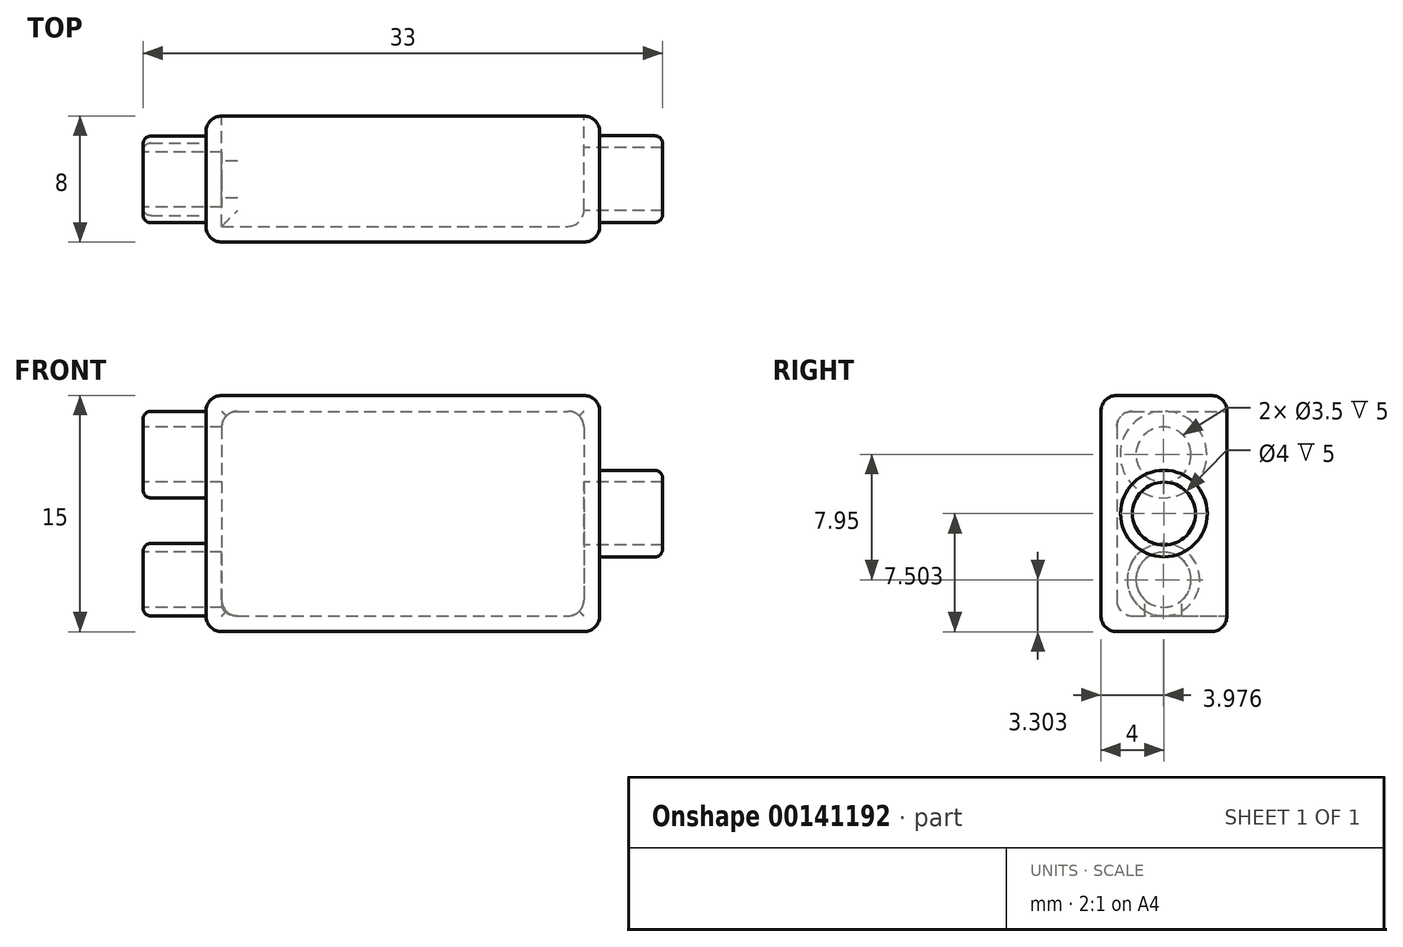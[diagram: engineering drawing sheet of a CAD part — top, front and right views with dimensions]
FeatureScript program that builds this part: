
annotation { "Feature Type Name" : "Feature", "Feature Type Description" : "" }
export const myFeature = defineFeature(function(context is Context, id is Id, definition is map)
    precondition{}
    {
        {
            var Q0;
            Q0=qCreatedBy(makeId("Front.planeOp"),FACE);
            var sketch = newSketch(context, id + "F0", { "sketchPlane" : qUnion([Q0])});
            skLineSegment(sketch, "E0.bottom", {"start": v(-13.07, 10.1) * mm, "end": v(11.93, 10.1) * mm});
            skLineSegment(sketch, "E0.top", {"start": v(-13.07, -4.9) * mm, "end": v(11.93, -4.9) * mm});
            skLineSegment(sketch, "E0.left", {"start": v(-13.07, 10.1) * mm, "end": v(-13.07, -4.9) * mm});
            skLineSegment(sketch, "E0.right", {"start": v(11.93, 10.1) * mm, "end": v(11.93, -4.9) * mm});
            skSolve(sketch);
        }
        {
            var Q0;
            Q0=makeQuery(id+"F0.imprint","IMPRINT",FACE,{"disambiguationData":[TD([[makeQuery(id+"F0.imprint","IMPRINT",EDGE,{"derivedFrom":sQuery(id+"F0.wireOp",EDGE,"E0.bottom")}),-1.0]])]});
            extrude(context, id + "F1", {"entities" : qUnion([Q0]), "depth" : 8 * mm});
        }
        {
            var Q0;
            Q0=makeQuery(id+"F1.opExtrude","CAP_FACE",FACE,{"disambiguationData":[OSD([sQuery(id+"F0.wireOp",EDGE,"E0.bottom"),sQuery(id+"F0.wireOp",EDGE,"E0.top"),sQuery(id+"F0.wireOp",EDGE,"E0.left"),sQuery(id+"F0.wireOp",EDGE,"E0.right")])],"isStart":true});
            shell(context, id + "F2", {"entities" : qUnion([Q0]), "thickness" : 1 * mm});
        }
        {
            var Q0;
            Q0=makeQuery(id+"F1.opExtrude","SWEPT_FACE",FACE,{"disambiguationData":[OSD([sQuery(id+"F0.wireOp",EDGE,"E0.right")])]});
            var sketch = newSketch(context, id + "F3", { "sketchPlane" : qUnion([Q0])});
            skPoint(sketch, "E1", {"position": v(-4, 2.6) * mm});
            skPoint(sketch, "E1.positionSnap0", {"position": v(-4, -4.9) * mm});
            skPoint(sketch, "E1.positionSnap1", {"position": v(0, 2.6) * mm});
            skCircle(sketch, "E2", {"center": v(-4, 2.6) * mm, "radius": 2.75 * mm});
            skSolve(sketch);
        }
        {
            var Q0;
            Q0=makeQuery(id+"F3.imprint","IMPRINT",FACE,{"disambiguationData":[TD([[makeQuery(id+"F3.imprint","IMPRINT",EDGE,{"derivedFrom":sQuery(id+"F3.wireOp",EDGE,"E2")}),1.0]])]});
            extrude(context, id + "F4", {"entities" : qUnion([Q0]), "operationType" : NewBodyOperationType.ADD, "depth" : 4 * mm});
        }
        {
            var Q0;
            Q0=makeQuery(id+"F4.opExtrude","CAP_FACE",FACE,{"disambiguationData":[OSD([sQuery(id+"F3.wireOp",EDGE,"E2")])],"isStart":false});
            shell(context, id + "F5", {"entities" : qUnion([Q0]), "thickness" : .75 * mm});
        }
        {
            var Q0;
            Q0=makeQuery(id+"F1.opExtrude","SWEPT_FACE",FACE,{"disambiguationData":[OSD([sQuery(id+"F0.wireOp",EDGE,"E0.left")])]});
            var sketch = newSketch(context, id + "F6", { "sketchPlane" : qUnion([Q0])});
            skPoint(sketch, "E3", {"position": v(4.02, 6.34) * mm});
            skPoint(sketch, "E3.positionSnap0", {"position": v(4.02, 5.16) * mm});
            skPoint(sketch, "E4", {"position": v(4.02, -1.6) * mm});
            skCircle(sketch, "E5", {"center": v(4.02, 6.34) * mm, "radius": 2.75 * mm});
            skCircle(sketch, "E6", {"center": v(4.02, -1.6) * mm, "radius": 2.3 * mm});
            skSolve(sketch);
        }
        {
            var Q0;
            Q0=makeQuery(id+"F5.opShell","OFFSET_FACE",FACE,{"disambiguationData":[OSD([sQuery(id+"F0.wireOp",EDGE,"E0.right")])]});
            extrude(context, id + "F7", {"entities" : qUnion([Q0]), "operationType" : NewBodyOperationType.REMOVE, "oppositeDirection" : true, "depth" : 10 * mm});
        }
        {
            var Q0;
            Q0=makeQuery(id+"F6.imprint","IMPRINT",FACE,{"disambiguationData":[TD([[makeQuery(id+"F6.imprint","IMPRINT",EDGE,{"derivedFrom":sQuery(id+"F6.wireOp",EDGE,"E6")}),1.0]])]});
            extrude(context, id + "F8", {"entities" : qUnion([Q0]), "operationType" : NewBodyOperationType.ADD, "depth" : 4 * mm});
        }
        {
            var Q0;
            Q0=makeQuery(id+"F6.imprint","IMPRINT",FACE,{"disambiguationData":[TD([[makeQuery(id+"F6.imprint","IMPRINT",EDGE,{"derivedFrom":sQuery(id+"F6.wireOp",EDGE,"E5")}),1.0]])]});
            extrude(context, id + "F9", {"entities" : qUnion([Q0]), "operationType" : NewBodyOperationType.ADD, "depth" : 4 * mm});
        }
        {
            var Q0;
            Q0=makeQuery(id+"F9.opExtrude","CAP_FACE",FACE,{"disambiguationData":[OSD([sQuery(id+"F6.wireOp",EDGE,"E5")])],"isStart":false});
            var sketch = newSketch(context, id + "F10", { "sketchPlane" : qUnion([Q0])});
            skCircle(sketch, "E7", {"center": v(4.02, 6.34) * mm, "radius": 1.75 * mm});
            skSolve(sketch);
        }
        {
            var Q0;
            Q0=makeQuery(id+"F10.imprint","IMPRINT",FACE,{"disambiguationData":[TD([[makeQuery(id+"F10.imprint","IMPRINT",EDGE,{"derivedFrom":sQuery(id+"F10.wireOp",EDGE,"E7")}),1.0]])]});
            extrude(context, id + "F11", {"entities" : qUnion([Q0]), "operationType" : NewBodyOperationType.REMOVE, "oppositeDirection" : true, "depth" : 10 * mm});
        }
        {
            var Q0;
            Q0=makeQuery(id+"F8.opExtrude","CAP_FACE",FACE,{"disambiguationData":[OSD([sQuery(id+"F6.wireOp",EDGE,"E6")])],"isStart":false});
            var sketch = newSketch(context, id + "F12", { "sketchPlane" : qUnion([Q0])});
            skCircle(sketch, "E8", {"center": v(4.02, -1.6) * mm, "radius": 1.75 * mm});
            skSolve(sketch);
        }
        {
            var Q0;
            Q0=makeQuery(id+"F12.imprint","IMPRINT",FACE,{"disambiguationData":[TD([[makeQuery(id+"F12.imprint","IMPRINT",EDGE,{"derivedFrom":sQuery(id+"F12.wireOp",EDGE,"E8")}),1.0]])]});
            extrude(context, id + "F13", {"entities" : qUnion([Q0]), "operationType" : NewBodyOperationType.REMOVE, "oppositeDirection" : true, "depth" : 10 * mm});
        }
        {
            var Q0;
            Q0=makeQuery(id+"F4.opExtrude","CAP_FACE",FACE,{"disambiguationData":[OSD([sQuery(id+"F3.wireOp",EDGE,"E2")])],"isStart":false});
            var sketch = newSketch(context, id + "F14", { "sketchPlane" : qUnion([Q0])});
            skSolve(sketch);
        }
        {
            var Q0;
            Q0=makeQuery(id+"F1.opExtrude","SWEPT_EDGE",EDGE,{"disambiguationData":[OSD([sQuery(id+"F0.wireOp",EDGE,"E0.bottom"),sQuery(id+"F0.wireOp",EDGE,"E0.right")])]});
            var Q1;
            Q1=makeQuery(id+"F1.opExtrude","CAP_EDGE",EDGE,{"disambiguationData":[OSD([sQuery(id+"F0.wireOp",EDGE,"E0.right")])],"isStart":false});
            var Q2;
            Q2=makeQuery(id+"F1.opExtrude","SWEPT_EDGE",EDGE,{"disambiguationData":[OSD([sQuery(id+"F0.wireOp",EDGE,"E0.top"),sQuery(id+"F0.wireOp",EDGE,"E0.right")])]});
            fillet(context, id + "F15", {"entities" : qUnion([Q0, Q1, Q2]), "radius" : 1 * mm, "tangentPropagation" : true, "allowEdgeOverflow" : false});
        }
        {
            var Q0;
            Q0=makeQuery(id+"F4.opExtrude","CAP_EDGE",EDGE,{"disambiguationData":[OSD([sQuery(id+"F3.wireOp",EDGE,"E2")])],"isStart":false});
            fillet(context, id + "F16", {"entities" : qUnion([Q0]), "radius" : .5 * mm, "tangentPropagation" : true, "allowEdgeOverflow" : false});
        }
        {
            var Q0;
            Q0=makeQuery(id+"F1.opExtrude","CAP_EDGE",EDGE,{"disambiguationData":[OSD([sQuery(id+"F0.wireOp",EDGE,"E0.bottom")])],"isStart":true});
            var Q1;
            Q1=makeQuery(id+"F1.opExtrude","CAP_EDGE",EDGE,{"disambiguationData":[OSD([sQuery(id+"F0.wireOp",EDGE,"E0.bottom")])],"isStart":false});
            var Q2;
            Q2=makeQuery(id+"F1.opExtrude","CAP_EDGE",EDGE,{"disambiguationData":[OSD([sQuery(id+"F0.wireOp",EDGE,"E0.top")])],"isStart":false});
            var Q3;
            Q3=makeQuery(id+"F1.opExtrude","CAP_EDGE",EDGE,{"disambiguationData":[OSD([sQuery(id+"F0.wireOp",EDGE,"E0.top")])],"isStart":true});
            fillet(context, id + "F17", {"entities" : qUnion([Q0, Q1, Q2, Q3]), "radius" : 1 * mm, "tangentPropagation" : true, "allowEdgeOverflow" : false});
        }
        {
            var Q0;
            Q0=makeQuery(id+"F1.opExtrude","SWEPT_EDGE",EDGE,{"disambiguationData":[OSD([sQuery(id+"F0.wireOp",EDGE,"E0.top"),sQuery(id+"F0.wireOp",EDGE,"E0.left")])]});
            var Q1;
            Q1=makeQuery(id+"F1.opExtrude","CAP_EDGE",EDGE,{"disambiguationData":[OSD([sQuery(id+"F0.wireOp",EDGE,"E0.left")])],"isStart":false});
            var Q2;
            Q2=makeQuery(id+"F1.opExtrude","SWEPT_EDGE",EDGE,{"disambiguationData":[OSD([sQuery(id+"F0.wireOp",EDGE,"E0.bottom"),sQuery(id+"F0.wireOp",EDGE,"E0.left")])]});
            fillet(context, id + "F18", {"entities" : qUnion([Q0, Q1, Q2]), "radius" : 1 * mm, "tangentPropagation" : true, "allowEdgeOverflow" : false});
        }
        {
            var Q0;
            Q0=makeQuery(id+"F8.opExtrude","CAP_EDGE",EDGE,{"disambiguationData":[OSD([sQuery(id+"F6.wireOp",EDGE,"E6")])],"isStart":false});
            fillet(context, id + "F19", {"entities" : qUnion([Q0]), "radius" : .5 * mm, "tangentPropagation" : true, "allowEdgeOverflow" : false});
        }
        {
            var Q0;
            Q0=makeQuery(id+"F9.opExtrude","CAP_EDGE",EDGE,{"disambiguationData":[OSD([sQuery(id+"F6.wireOp",EDGE,"E5")])],"isStart":false});
            fillet(context, id + "F20", {"entities" : qUnion([Q0]), "radius" : .5 * mm, "tangentPropagation" : true, "allowEdgeOverflow" : false});
        }
        {
            var Q0;
            Q0=makeQuery(id+"F2.opShell","OFFSET_EDGE",EDGE,{"disambiguationData":[OSD([sQuery(id+"F0.wireOp",EDGE,"E0.bottom"),sQuery(id+"F0.wireOp",EDGE,"E0.left")])]});
            var Q1;
            {var subQ0=sQuery(id+"F0.wireOp",EDGE,"E0.bottom");Q1=makeQuery(id+"F2.opShell","OFFSET_EDGE",EDGE,{"disambiguationData":[OSD([subQ0]),TDD([makeQuery(id+"F1.opExtrude","CAP_EDGE",EDGE,{"disambiguationData":[OSD([subQ0])],"isStart":false})])]});}
            var Q2;
            Q2=makeQuery(id+"F2.opShell","OFFSET_EDGE",EDGE,{"disambiguationData":[OSD([sQuery(id+"F0.wireOp",EDGE,"E0.bottom"),sQuery(id+"F0.wireOp",EDGE,"E0.right")])]});
            var Q3;
            {var subQ0=sQuery(id+"F0.wireOp",EDGE,"E0.right");Q3=makeQuery(id+"F2.opShell","OFFSET_EDGE",EDGE,{"disambiguationData":[OSD([subQ0]),TDD([makeQuery(id+"F1.opExtrude","CAP_EDGE",EDGE,{"disambiguationData":[OSD([subQ0])],"isStart":false})])]});}
            var Q4;
            Q4=makeQuery(id+"F2.opShell","OFFSET_EDGE",EDGE,{"disambiguationData":[OSD([sQuery(id+"F0.wireOp",EDGE,"E0.top"),sQuery(id+"F0.wireOp",EDGE,"E0.right")])]});
            var Q5;
            {var subQ0=sQuery(id+"F0.wireOp",EDGE,"E0.top");Q5=makeQuery(id+"F2.opShell","OFFSET_EDGE",EDGE,{"disambiguationData":[OSD([subQ0]),TDD([makeQuery(id+"F1.opExtrude","CAP_EDGE",EDGE,{"disambiguationData":[OSD([subQ0])],"isStart":false})])]});}
            var Q6;
            Q6=makeQuery(id+"F2.opShell","OFFSET_EDGE",EDGE,{"disambiguationData":[OSD([sQuery(id+"F0.wireOp",EDGE,"E0.top"),sQuery(id+"F0.wireOp",EDGE,"E0.left")])]});
            fillet(context, id + "F21", {"entities" : qUnion([Q0, Q1, Q2, Q3, Q4, Q5, Q6]), "radius" : 1 * mm, "tangentPropagation" : true, "allowEdgeOverflow" : false});
        }
    });
